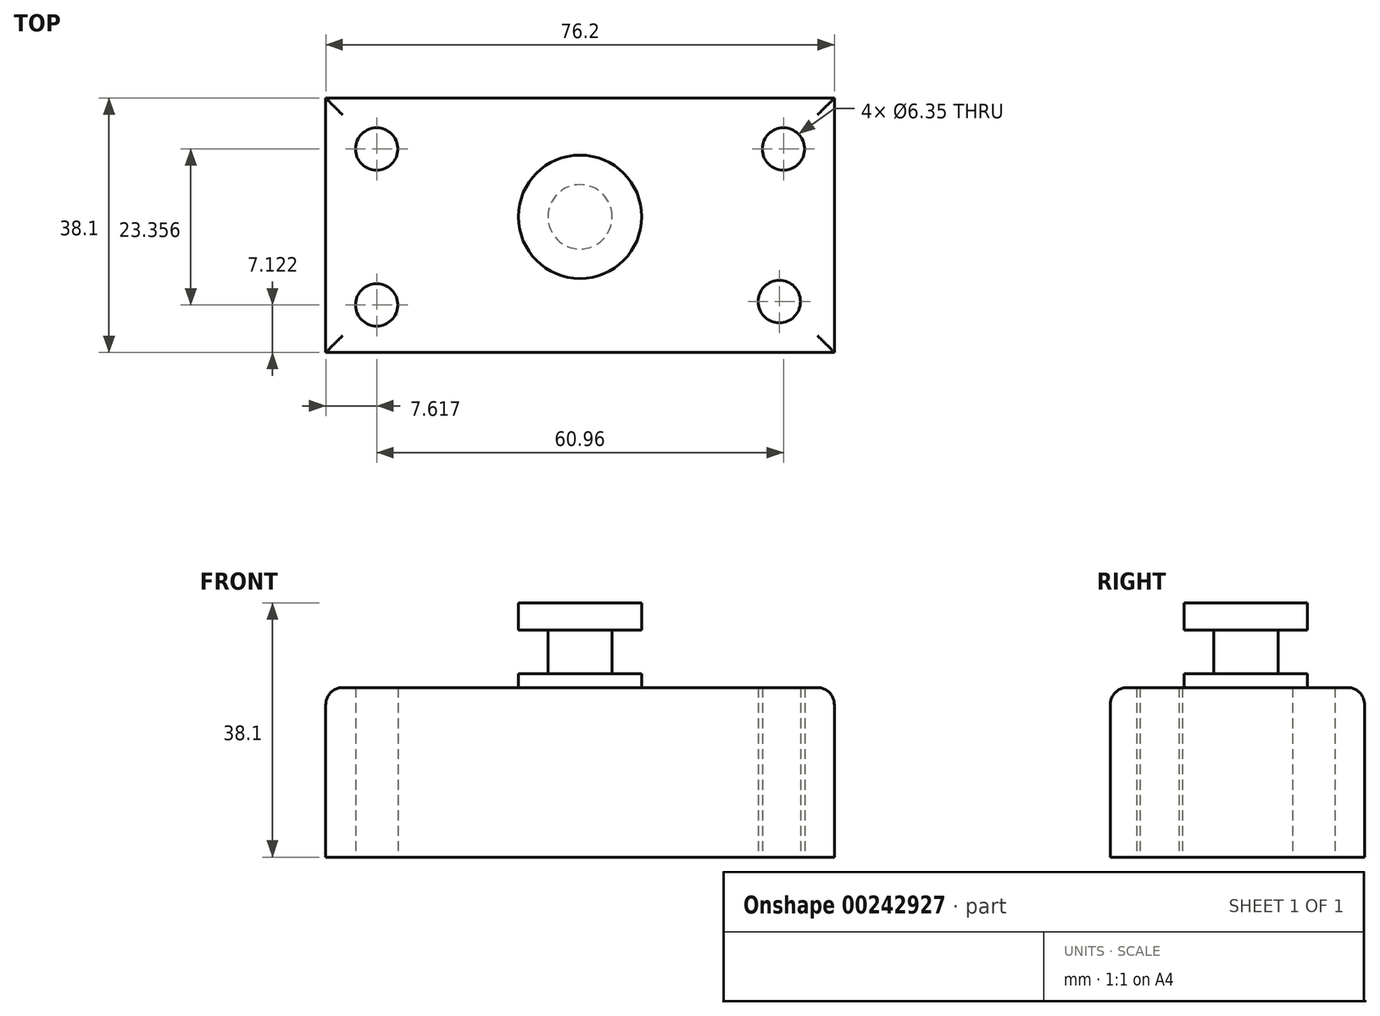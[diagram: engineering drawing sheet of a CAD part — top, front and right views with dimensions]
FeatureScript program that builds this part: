
annotation { "Feature Type Name" : "Feature", "Feature Type Description" : "" }
export const myFeature = defineFeature(function(context is Context, id is Id, definition is map)
    precondition{}
    {
        {
            var Q0;
            Q0=qCreatedBy(makeId("Top.planeOp"),FACE);
            var sketch = newSketch(context, id + "F0", { "sketchPlane" : qUnion([Q0])});
            skLineSegment(sketch, "E0.bottom", {"start": v(-37.7, 16.55) * mm, "end": v(38.5, 16.55) * mm});
            skLineSegment(sketch, "E0.top", {"start": v(-37.7, -21.55) * mm, "end": v(38.5, -21.55) * mm});
            skLineSegment(sketch, "E0.left", {"start": v(-37.7, 16.55) * mm, "end": v(-37.7, -21.55) * mm});
            skLineSegment(sketch, "E0.right", {"start": v(38.5, 16.55) * mm, "end": v(38.5, -21.55) * mm});
            skSolve(sketch);
        }
        {
            var Q0;
            Q0 = qSketchRegion(id + "F0", true);
            extrude(context, id + "F1", {"entities" : qUnion([Q0]), "depth" : 25.4 * mm});
        }
        {
            var Q0;
            Q0=qCreatedBy(makeId("Top.planeOp"),FACE);
            var sketch = newSketch(context, id + "F2", { "sketchPlane" : qUnion([Q0])});
            skCircle(sketch, "E1", {"center": v(-30.08, 8.93) * mm, "radius": 3.18 * mm});
            skCircle(sketch, "E2", {"center": v(-30.08, -14.43) * mm, "radius": 3.18 * mm});
            skCircle(sketch, "E3", {"center": v(30.26, -13.93) * mm, "radius": 3.18 * mm});
            skCircle(sketch, "E4", {"center": v(30.88, 8.93) * mm, "radius": 3.18 * mm});
            skSolve(sketch);
        }
        {
            var Q0;
            Q0 = qSketchRegion(id + "F2", true);
            extrude(context, id + "F3", {"entities" : qUnion([Q0]), "operationType" : NewBodyOperationType.REMOVE, "depth" : 38.1 * mm});
        }
        {
            var Q0;
            Q0=qCreatedBy(makeId("Top.planeOp"),FACE);
            var sketch = newSketch(context, id + "F4", { "sketchPlane" : qUnion([Q0])});
            skCircle(sketch, "E5", {"center": v(0.4, -1.23) * mm, "radius": 9.24 * mm});
            skSolve(sketch);
        }
        {
            var Q0;
            Q0 = qSketchRegion(id + "F4", true);
            extrude(context, id + "F5", {"entities" : qUnion([Q0]), "operationType" : NewBodyOperationType.ADD, "depth" : 38.1 * mm});
        }
        {
            var Q0;
            Q0=makeQuery(id+"F1.opExtrude","CAP_EDGE",EDGE,{"disambiguationData":[OSD([sQuery(id+"F0.wireOp",EDGE,"E0.top")])],"isStart":false});
            var Q1;
            Q1=makeQuery(id+"F1.opExtrude","CAP_EDGE",EDGE,{"disambiguationData":[OSD([sQuery(id+"F0.wireOp",EDGE,"E0.left")])],"isStart":false});
            var Q2;
            Q2=makeQuery(id+"F1.opExtrude","CAP_EDGE",EDGE,{"disambiguationData":[OSD([sQuery(id+"F0.wireOp",EDGE,"E0.bottom")])],"isStart":false});
            var Q3;
            Q3=makeQuery(id+"F1.opExtrude","CAP_EDGE",EDGE,{"disambiguationData":[OSD([sQuery(id+"F0.wireOp",EDGE,"E0.right")])],"isStart":false});
            fillet(context, id + "F6", {"entities" : qUnion([Q0, Q1, Q2, Q3]), "radius" : 2.54 * mm, "tangentPropagation" : true, "allowEdgeOverflow" : false});
        }
        {
            var Q0;
            Q0=qCreatedBy(makeId("Front.planeOp"),FACE);
            var sketch = newSketch(context, id + "F7", { "sketchPlane" : qUnion([Q0])});
            skLineSegment(sketch, "E6.bottom", {"start": v(-13.1, 34) * mm, "end": v(-4.26, 34) * mm});
            skLineSegment(sketch, "E6.top", {"start": v(-13.1, 27.48) * mm, "end": v(-4.26, 27.48) * mm});
            skLineSegment(sketch, "E6.left", {"start": v(-13.1, 34) * mm, "end": v(-13.1, 27.48) * mm});
            skLineSegment(sketch, "E6.right", {"start": v(-4.26, 34) * mm, "end": v(-4.26, 27.48) * mm});
            skSolve(sketch);
        }
        {
            var Q0;
            Q0 = qSketchRegion(id + "F7", true);
            var Q1;
            Q1=makeQuery(id+"F5.opExtrude","SWEPT_FACE",FACE,{"disambiguationData":[OSD([sQuery(id+"F4.wireOp",EDGE,"E5")])]});
            revolve(context, id + "F8", {"operationType" : NewBodyOperationType.REMOVE, "entities" : qUnion([Q0]), "axis" : qUnion([Q1]), "revolveType" : RevolveType.FULL, "oppositeDirection" : true});
        }
    });
